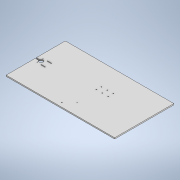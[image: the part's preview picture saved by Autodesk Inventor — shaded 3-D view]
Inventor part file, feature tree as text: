
AUTODESK INVENTOR PART (.ipt)
format: ipt  version: 2021.1 (Build 251245010, 245A)  size: 222,208 bytes
history: native  units: mm
features: extrude x4, sketch x4, other x1
ambient origin geometry x8: Origin, YZ Plane, XZ Plane, XY Plane, X Axis, Y Axis, Z Axis, Center Point
bodies: Body1 (feature_tree)
feature tree (9):
  other  "Твердое тело1"
  extrude  "Выдавливание1"  Depth=275.0mm
  extrude  "Выдавливание2"  Depth=150.0mm
  extrude  "Выдавливание3"  Depth=6.0mm TaperAngle=0.0deg
  extrude  "Выдавливание4"  TaperAngle=135.0deg  [1 undecoded]
  sketch  "Эскиз1"
  sketch  "Эскиз2"
  sketch  "Эскиз3"
  sketch  "Эскиз4"
note: 1 required parameter value undecoded (feature->parameter linkage not recoverable at this tier; creation-order binding heuristic only, values carry confidence <= 0.55)
